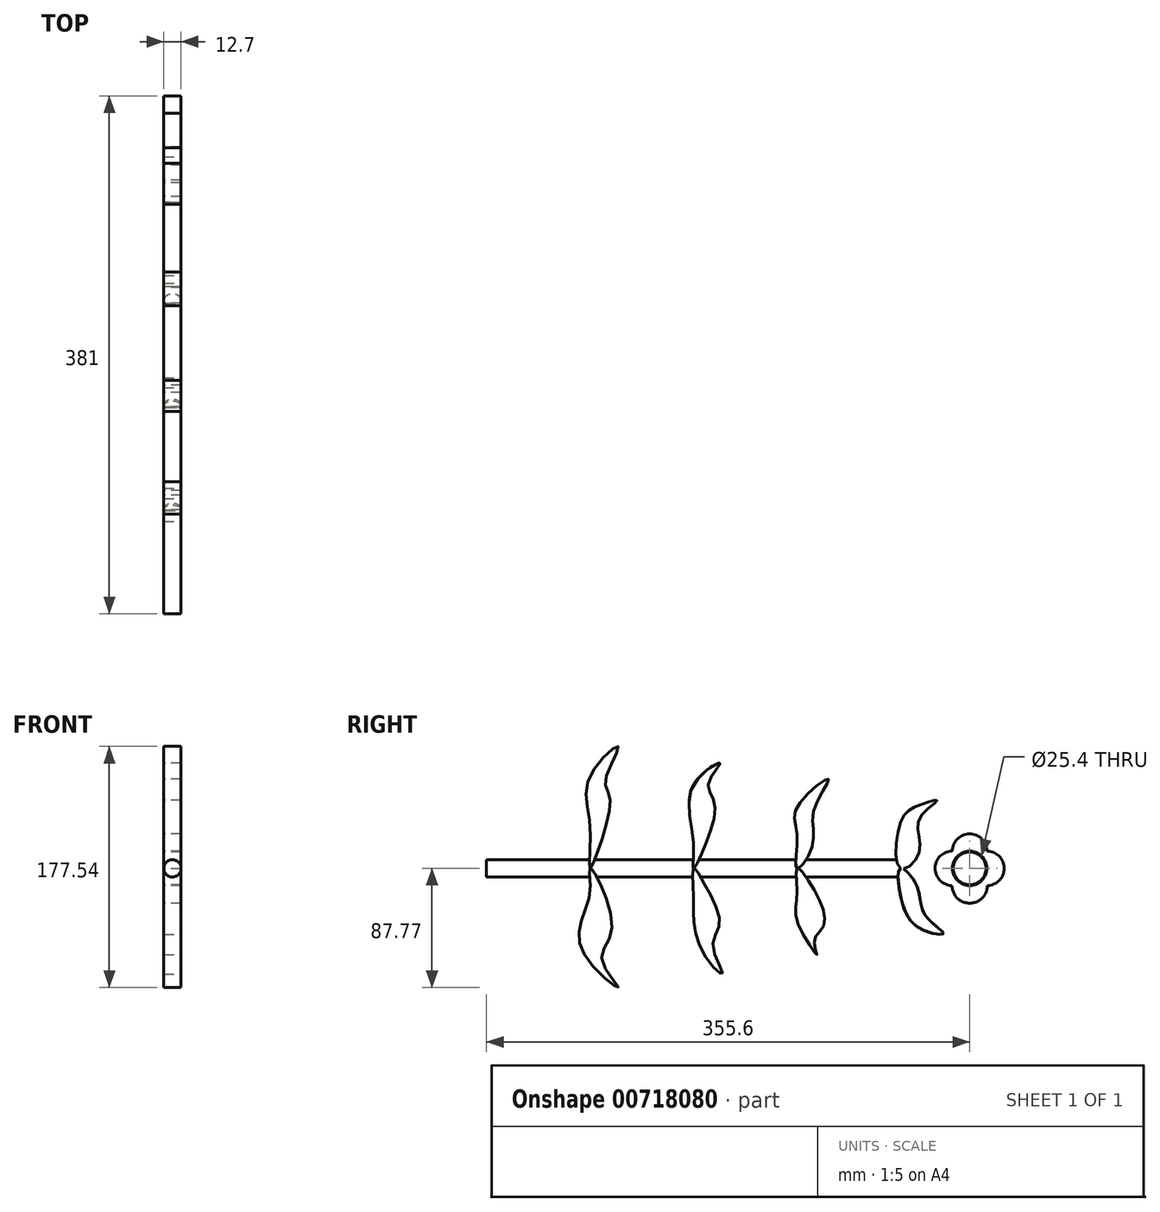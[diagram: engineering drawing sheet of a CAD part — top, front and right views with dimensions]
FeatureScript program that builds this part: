
annotation { "Feature Type Name" : "Feature", "Feature Type Description" : "" }
export const myFeature = defineFeature(function(context is Context, id is Id, definition is map)
    precondition{}
    {
        {
            var Q0;
            Q0=qCreatedBy(makeId("Front.planeOp"),FACE);
            var sketch = newSketch(context, id + "F0", { "sketchPlane" : qUnion([Q0])});
            skCircle(sketch, "E0", {"center": v(0, 0) * mm, "radius": 6.35 * mm});
            skSolve(sketch);
        }
        {
            var Q0;
            Q0 = qSketchRegion(id + "F0", true);
            extrude(context, id + "F1", {"entities" : qUnion([Q0]), "endBound" : BoundingType.SYMMETRIC, "depth" : 304.8 * mm, "offsetDistance" : 25.4 * mm});
        }
        {
            var Q0;
            Q0=qCreatedBy(makeId("Right.planeOp"),FACE);
            var sketch = newSketch(context, id + "F2", { "sketchPlane" : qUnion([Q0])});
            skLineSegment(sketch, "E1", {"start": v(0, 0) * mm, "end": v(-152.4, 0) * mm, "construction": true});
            skLineSegment(sketch, "E2", {"start": v(0, 0) * mm, "end": v(152.4, 0) * mm, "construction": true});
            skPoint(sketch, "E3.5.internal.snap0", {"position": v(-76.2, 0) * mm});
            skPoint(sketch, "E3.7.internal.snap0", {"position": v(-76.2, 0) * mm});
            skFitSpline(sketch, "E3", {"points": [v(-76.2, 0) * mm, v(-69.1, -10.63) * mm, v(-60.59, -48.27) * mm, v(-67.53, -67.49) * mm, v(-55.4, -87.64) * mm, v(-76.2, -69.62) * mm, v(-83.91, -43.55) * mm, v(-76.2, -17.25) * mm, v(-76.2, 0) * mm]});
            skFitSpline(sketch, "E4", {"points": [v(-76.2, 0) * mm, v(-68.95, 16.85) * mm, v(-61.74, 52.36) * mm, v(-64.8, 65.57) * mm, v(-55.44, 89.56) * mm, v(-76.2, 68.18) * mm, v(-76.2, 30.98) * mm, v(-76.2, 0) * mm]});
            skFitSpline(sketch, "E5", {"points": [v(0, 0) * mm, v(8.33, -11.97) * mm, v(19.12, -40.6) * mm, v(14.22, -57.9) * mm, v(21.28, -77.55) * mm, v(8.53, -65) * mm, v(0, -35.1) * mm, v(0, -20.21) * mm, v(0, 0) * mm]});
            skFitSpline(sketch, "E6", {"points": [v(0, 0) * mm, v(8.74, 17.41) * mm, v(15.25, 48.91) * mm, v(10.9, 63.17) * mm, v(19.45, 77.19) * mm, v(0, 61.65) * mm, v(0, 18.81) * mm, v(0, 0) * mm]});
            skPoint(sketch, "E7.5.internal.snap0", {"position": v(76.2, 0) * mm});
            skPoint(sketch, "E7.6.internal.snap0", {"position": v(76.2, 0) * mm});
            skFitSpline(sketch, "E7", {"points": [v(76.2, 0) * mm, v(87.54, -13.94) * mm, v(96.06, -41.4) * mm, v(88.8, -53.17) * mm, v(90.76, -63.48) * mm, v(76.2, -38.61) * mm, v(76.2, -19.7) * mm, v(76.2, 0) * mm]});
            skFitSpline(sketch, "E8", {"points": [v(76.2, 0) * mm, v(87.54, 16.8) * mm, v(88.8, 43.51) * mm, v(99.01, 65.68) * mm, v(76.2, 45.18) * mm, v(76.2, 23.96) * mm, v(76.2, 0) * mm]});
            skFitSpline(sketch, "E9", {"points": [v(152.4, 0) * mm, v(164.55, -13.41) * mm, v(170.6, -34.75) * mm, v(183.88, -48.02) * mm, v(166.1, -44) * mm, v(152.4, -20.52) * mm, v(152.4, 0) * mm]});
            skFitSpline(sketch, "E10", {"points": [v(152.4, 0) * mm, v(166.1, 12.2) * mm, v(166.1, 36.13) * mm, v(179.14, 49.88) * mm, v(166.1, 46.57) * mm, v(152.4, 34.24) * mm, v(152.4, 0) * mm]});
            skSolve(sketch);
        }
        {
            var Q0;
            Q0=qCreatedBy(makeId("Right.planeOp"),FACE);
            var sketch = newSketch(context, id + "F3", { "sketchPlane" : qUnion([Q0])});
            skCircle(sketch, "E11", {"center": v(203.2, 0) * mm, "radius": 12.7 * mm});
            skCircle(sketch, "E12", {"center": v(203.2, -12.7) * mm, "radius": 12.95 * mm});
            skCircle(sketch, "E13", {"center": v(203.2, 12.7) * mm, "radius": 12.7 * mm});
            skCircle(sketch, "E14", {"center": v(215.9, 0) * mm, "radius": 12.7 * mm});
            skCircle(sketch, "E15", {"center": v(190.5, 0) * mm, "radius": 12.7 * mm});
            skSolve(sketch);
        }
        {
            var Q0;
            Q0 = qSketchRegion(id + "F3", true);
            extrude(context, id + "F4", {"entities" : qUnion([Q0]), "endBound" : BoundingType.SYMMETRIC, "depth" : 12.7 * mm, "offsetDistance" : 25.4 * mm});
        }
        {
            var Q0;
            Q0 = qSketchRegion(id + "F2", true);
            extrude(context, id + "F5", {"entities" : qUnion([Q0]), "operationType" : NewBodyOperationType.ADD, "endBound" : BoundingType.SYMMETRIC, "depth" : 12.7 * mm, "offsetDistance" : 25.4 * mm});
        }
        {
            var Q0;
            Q0=qCreatedBy(makeId("Right.planeOp"),FACE);
            var sketch = newSketch(context, id + "F6", { "sketchPlane" : qUnion([Q0])});
            skCircle(sketch, "E16", {"center": v(203.2, 0) * mm, "radius": 12.06 * mm});
            skSolve(sketch);
        }
        {
            var Q0;
            Q0 = qSketchRegion(id + "F6", true);
            extrude(context, id + "F7", {"entities" : qUnion([Q0]), "endBound" : BoundingType.SYMMETRIC, "depth" : 12.7 * mm, "offsetDistance" : 25.4 * mm});
        }
    });
